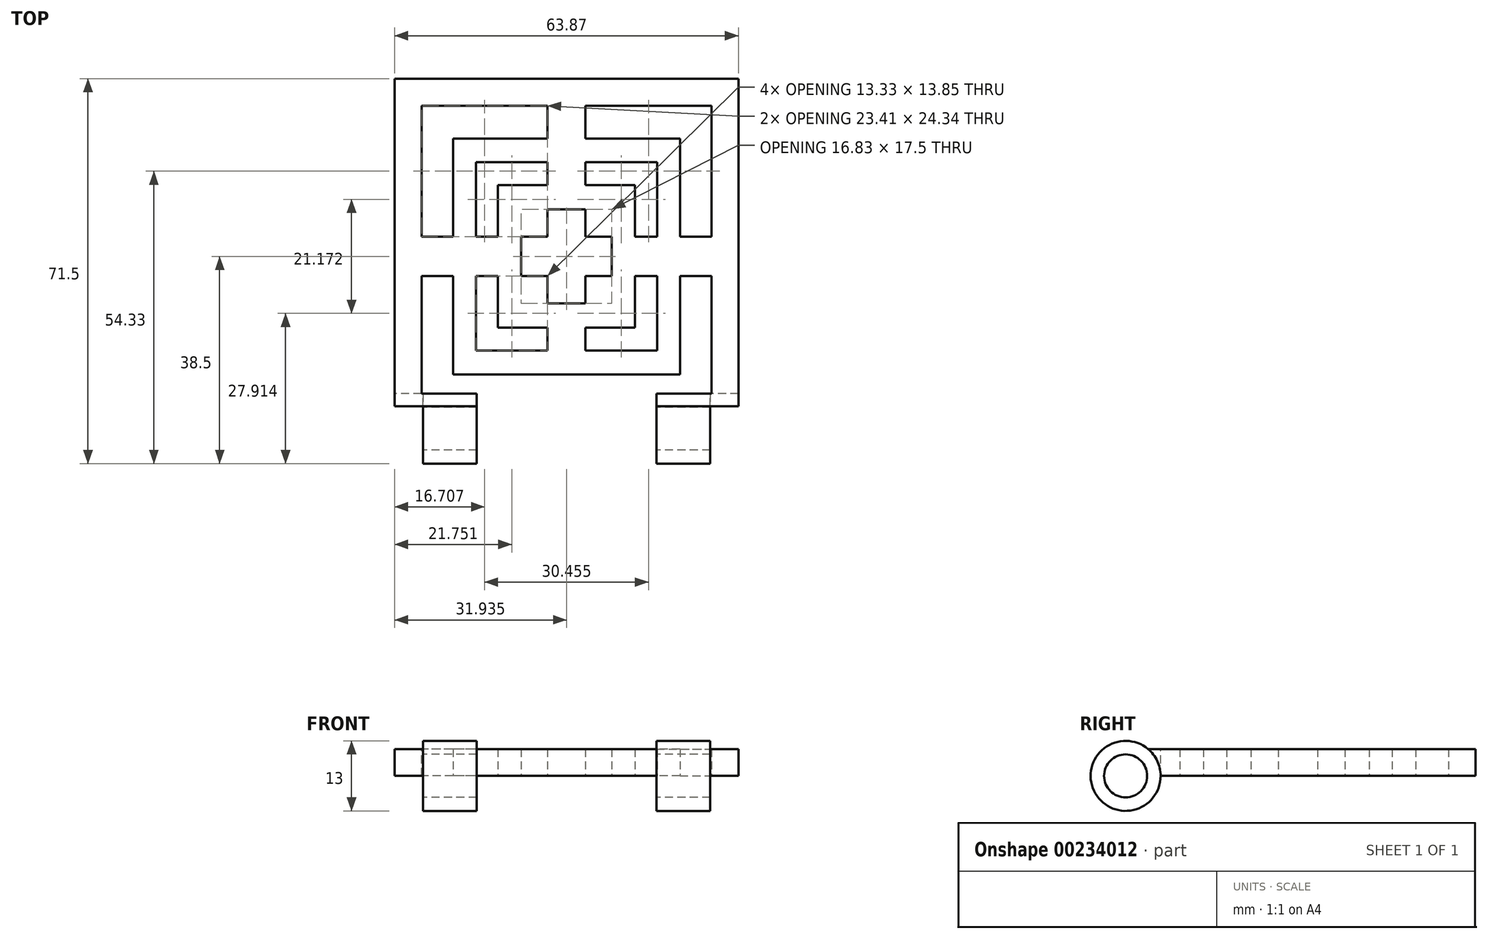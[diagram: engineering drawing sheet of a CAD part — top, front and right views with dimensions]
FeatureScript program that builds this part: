
annotation { "Feature Type Name" : "Feature", "Feature Type Description" : "" }
export const myFeature = defineFeature(function(context is Context, id is Id, definition is map)
    precondition{}
    {
        {
            var Q0;
            Q0=qCreatedBy(makeId("Top.planeOp"),FACE);
            var sketch = newSketch(context, id + "F0", { "sketchPlane" : qUnion([Q0])});
            skLineSegment(sketch, "E0.bottom", {"start": v(0, 0) * mm, "end": v(63.87, 0) * mm});
            skLineSegment(sketch, "E0.top", {"start": v(0, 61) * mm, "end": v(63.87, 61) * mm});
            skLineSegment(sketch, "E0.left", {"start": v(0, 0) * mm, "end": v(0, 61) * mm});
            skLineSegment(sketch, "E0.right", {"start": v(63.87, 0) * mm, "end": v(63.87, 61) * mm});
            skLineSegment(sketch, "E1.bottom", {"start": v(5, 0) * mm, "end": v(58.87, 0) * mm});
            skLineSegment(sketch, "E1.left", {"start": v(5, 0) * mm, "end": v(5, 56) * mm});
            skLineSegment(sketch, "E1.right", {"start": v(58.87, 0) * mm, "end": v(58.87, 56) * mm});
            skLineSegment(sketch, "E2", {"start": v(5, 56) * mm, "end": v(58.87, 56) * mm});
            skLineSegment(sketch, "E3", {"start": v(5, 56) * mm, "end": v(58.87, 0) * mm, "construction": true});
            skLineSegment(sketch, "E4", {"start": v(58.87, 56) * mm, "end": v(5, 0) * mm, "construction": true});
            skLineSegment(sketch, "E5.bottom", {"start": v(53, 49.9) * mm, "end": v(10.86, 49.9) * mm});
            skLineSegment(sketch, "E5.top", {"start": v(53, 6.1) * mm, "end": v(10.86, 6.1) * mm});
            skLineSegment(sketch, "E5.left", {"start": v(53, 49.9) * mm, "end": v(53, 6.1) * mm});
            skLineSegment(sketch, "E5.right", {"start": v(10.86, 49.9) * mm, "end": v(10.86, 6.1) * mm});
            skPoint(sketch, "E5.middle", {"position": v(31.93, 28) * mm});
            skLineSegment(sketch, "E6.bottom", {"start": v(48.78, 45.51) * mm, "end": v(15.09, 45.51) * mm});
            skLineSegment(sketch, "E6.top", {"start": v(48.78, 10.49) * mm, "end": v(15.09, 10.49) * mm});
            skLineSegment(sketch, "E6.left", {"start": v(48.78, 45.51) * mm, "end": v(48.78, 10.49) * mm});
            skLineSegment(sketch, "E6.right", {"start": v(15.09, 45.51) * mm, "end": v(15.09, 10.49) * mm});
            skLineSegment(sketch, "E7.bottom", {"start": v(44.66, 41.23) * mm, "end": v(19.21, 41.23) * mm});
            skLineSegment(sketch, "E7.top", {"start": v(44.66, 14.77) * mm, "end": v(19.21, 14.77) * mm});
            skLineSegment(sketch, "E7.left", {"start": v(44.66, 41.23) * mm, "end": v(44.66, 14.77) * mm});
            skLineSegment(sketch, "E7.right", {"start": v(19.21, 41.23) * mm, "end": v(19.21, 14.77) * mm});
            skLineSegment(sketch, "E8.bottom", {"start": v(40.35, 36.75) * mm, "end": v(23.52, 36.75) * mm});
            skLineSegment(sketch, "E8.top", {"start": v(40.35, 19.25) * mm, "end": v(23.52, 19.25) * mm});
            skLineSegment(sketch, "E8.left", {"start": v(40.35, 36.75) * mm, "end": v(40.35, 19.25) * mm});
            skLineSegment(sketch, "E8.right", {"start": v(23.52, 36.75) * mm, "end": v(23.52, 19.25) * mm});
            skLineSegment(sketch, "E9.bottom", {"start": v(35.46, 31.66) * mm, "end": v(28.41, 31.66) * mm, "construction": true});
            skLineSegment(sketch, "E9.top", {"start": v(35.46, 24.34) * mm, "end": v(28.41, 24.34) * mm, "construction": true});
            skLineSegment(sketch, "E9.left", {"start": v(35.46, 31.66) * mm, "end": v(35.46, 24.34) * mm, "construction": true});
            skLineSegment(sketch, "E9.right", {"start": v(28.41, 31.66) * mm, "end": v(28.41, 24.34) * mm, "construction": true});
            skLineSegment(sketch, "E10.bottom", {"start": v(28.41, 31.66) * mm, "end": v(5, 31.66) * mm});
            skLineSegment(sketch, "E10.top", {"start": v(28.41, 24.34) * mm, "end": v(5, 24.34) * mm});
            skLineSegment(sketch, "E10.right", {"start": v(5, 31.66) * mm, "end": v(5, 24.34) * mm, "construction": true});
            skLineSegment(sketch, "E11.bottom", {"start": v(28.41, 24.34) * mm, "end": v(35.46, 24.34) * mm, "construction": true});
            skLineSegment(sketch, "E11.top", {"start": v(28.41, 0) * mm, "end": v(35.46, 0) * mm, "construction": true});
            skLineSegment(sketch, "E11.left", {"start": v(28.41, 24.34) * mm, "end": v(28.41, 0) * mm});
            skLineSegment(sketch, "E11.right", {"start": v(35.46, 24.34) * mm, "end": v(35.46, 0) * mm});
            skLineSegment(sketch, "E12.bottom", {"start": v(35.46, 31.66) * mm, "end": v(58.87, 31.66) * mm});
            skLineSegment(sketch, "E12.top", {"start": v(35.46, 24.34) * mm, "end": v(58.87, 24.34) * mm});
            skLineSegment(sketch, "E12.right", {"start": v(58.87, 31.66) * mm, "end": v(58.87, 24.34) * mm, "construction": true});
            skLineSegment(sketch, "E13.top", {"start": v(35.46, 56) * mm, "end": v(28.41, 56) * mm, "construction": true});
            skLineSegment(sketch, "E13.left", {"start": v(35.46, 31.66) * mm, "end": v(35.46, 56) * mm});
            skLineSegment(sketch, "E13.right", {"start": v(28.41, 31.66) * mm, "end": v(28.41, 56) * mm});
            skSolve(sketch);
        }
        {
            var Q0;
            Q0=makeQuery(id+"F0.imprint","IMPRINT",FACE,{"disambiguationData":[TD([[makeQuery(id+"F0.imprint","IMPRINT",EDGE,{"derivedFrom":sQuery(id+"F0.wireOp",EDGE,"E0.top")}),-1.0]])]});
            var Q1;
            {var subQ7=sQuery(id+"F0.wireOp",EDGE,"E5.right");var subQ8=sQuery(id+"F0.wireOp",EDGE,"E5.bottom");var subQ9=makeQuery(id+"F0.imprint","INTERSECT",VERTEX,{"derivedFrom":[subQ8,subQ7]});Q1=makeQuery(id+"F0.imprint","IMPRINT",FACE,{"disambiguationData":[TD([[makeQuery(id+"F0.imprint","IMPRINT",EDGE,{"disambiguationData":[TD([[subQ9,1.0]])],"derivedFrom":subQ8}),1.0]])]});}
            var Q2;
            {var subQ0=sQuery(id+"F0.wireOp",EDGE,"E13.left");var subQ1=sQuery(id+"F0.wireOp",EDGE,"E2");var subQ2=makeQuery(id+"F0.imprint","INTERSECT",VERTEX,{"derivedFrom":[subQ1,subQ0]});Q2=makeQuery(id+"F0.imprint","IMPRINT",FACE,{"disambiguationData":[TD([[makeQuery(id+"F0.imprint","IMPRINT",EDGE,{"disambiguationData":[TD([[subQ2,1.0]])],"derivedFrom":subQ1}),-1.0]])]});}
            var Q3;
            {var subQ5=sQuery(id+"F0.wireOp",EDGE,"E5.left");var subQ9=sQuery(id+"F0.wireOp",EDGE,"E5.bottom");var subQ10=makeQuery(id+"F0.imprint","INTERSECT",VERTEX,{"derivedFrom":[subQ9,subQ5]});Q3=makeQuery(id+"F0.imprint","IMPRINT",FACE,{"disambiguationData":[TD([[makeQuery(id+"F0.imprint","IMPRINT",EDGE,{"disambiguationData":[TD([[subQ10,-1.0]])],"derivedFrom":subQ9}),1.0]])]});}
            var Q4;
            {var subQ0=sQuery(id+"F0.wireOp",EDGE,"E13.left");var subQ1=sQuery(id+"F0.wireOp",EDGE,"E5.bottom");var subQ2=makeQuery(id+"F0.imprint","INTERSECT",VERTEX,{"derivedFrom":[subQ1,subQ0]});Q4=makeQuery(id+"F0.imprint","IMPRINT",FACE,{"disambiguationData":[TD([[makeQuery(id+"F0.imprint","IMPRINT",EDGE,{"disambiguationData":[TD([[subQ2,-1.0]])],"derivedFrom":subQ1}),1.0]])]});}
            var Q5;
            {var subQ0=sQuery(id+"F0.wireOp",EDGE,"E10.bottom");var subQ1=sQuery(id+"F0.wireOp",EDGE,"E5.right");var subQ2=makeQuery(id+"F0.imprint","INTERSECT",VERTEX,{"derivedFrom":[subQ1,subQ0]});Q5=makeQuery(id+"F0.imprint","IMPRINT",FACE,{"disambiguationData":[TD([[makeQuery(id+"F0.imprint","IMPRINT",EDGE,{"disambiguationData":[TD([[subQ2,-1.0]])],"derivedFrom":subQ1}),1.0]])]});}
            var Q6;
            {var subQ7=sQuery(id+"F0.wireOp",EDGE,"E5.right");var subQ8=sQuery(id+"F0.wireOp",EDGE,"E5.top");var subQ9=makeQuery(id+"F0.imprint","INTERSECT",VERTEX,{"derivedFrom":[subQ8,subQ7]});Q6=makeQuery(id+"F0.imprint","IMPRINT",FACE,{"disambiguationData":[TD([[makeQuery(id+"F0.imprint","IMPRINT",EDGE,{"disambiguationData":[TD([[subQ9,1.0]])],"derivedFrom":subQ8}),-1.0]])]});}
            var Q7;
            {var subQ0=sQuery(id+"F0.wireOp",EDGE,"E11.right");var subQ1=sQuery(id+"F0.wireOp",EDGE,"E5.top");var subQ2=makeQuery(id+"F0.imprint","INTERSECT",VERTEX,{"derivedFrom":[subQ1,subQ0]});Q7=makeQuery(id+"F0.imprint","IMPRINT",FACE,{"disambiguationData":[TD([[makeQuery(id+"F0.imprint","IMPRINT",EDGE,{"disambiguationData":[TD([[subQ2,-1.0]])],"derivedFrom":subQ1}),-1.0]])]});}
            var Q8;
            {var subQ6=sQuery(id+"F0.wireOp",EDGE,"E5.left");var subQ9=sQuery(id+"F0.wireOp",EDGE,"E5.top");var subQ10=makeQuery(id+"F0.imprint","INTERSECT",VERTEX,{"derivedFrom":[subQ9,subQ6]});Q8=makeQuery(id+"F0.imprint","IMPRINT",FACE,{"disambiguationData":[TD([[makeQuery(id+"F0.imprint","IMPRINT",EDGE,{"disambiguationData":[TD([[subQ10,-1.0]])],"derivedFrom":subQ9}),-1.0]])]});}
            var Q9;
            {var subQ0=sQuery(id+"F0.wireOp",EDGE,"E12.bottom");var subQ1=sQuery(id+"F0.wireOp",EDGE,"E5.left");var subQ2=makeQuery(id+"F0.imprint","INTERSECT",VERTEX,{"derivedFrom":[subQ1,subQ0]});Q9=makeQuery(id+"F0.imprint","IMPRINT",FACE,{"disambiguationData":[TD([[makeQuery(id+"F0.imprint","IMPRINT",EDGE,{"disambiguationData":[TD([[subQ2,-1.0]])],"derivedFrom":subQ1}),-1.0]])]});}
            var Q10;
            {var subQ5=sQuery(id+"F0.wireOp",EDGE,"E7.left");var subQ6=sQuery(id+"F0.wireOp",EDGE,"E7.bottom");var subQ7=makeQuery(id+"F0.imprint","INTERSECT",VERTEX,{"derivedFrom":[subQ6,subQ5]});Q10=makeQuery(id+"F0.imprint","IMPRINT",FACE,{"disambiguationData":[TD([[makeQuery(id+"F0.imprint","IMPRINT",EDGE,{"disambiguationData":[TD([[subQ7,-1.0]])],"derivedFrom":subQ6}),1.0]])]});}
            var Q11;
            {var subQ0=sQuery(id+"F0.wireOp",EDGE,"E12.bottom");var subQ1=sQuery(id+"F0.wireOp",EDGE,"E7.left");var subQ2=makeQuery(id+"F0.imprint","INTERSECT",VERTEX,{"derivedFrom":[subQ1,subQ0]});Q11=makeQuery(id+"F0.imprint","IMPRINT",FACE,{"disambiguationData":[TD([[makeQuery(id+"F0.imprint","IMPRINT",EDGE,{"disambiguationData":[TD([[subQ2,-1.0]])],"derivedFrom":subQ1}),-1.0]])]});}
            var Q12;
            {var subQ7=sQuery(id+"F0.wireOp",EDGE,"E7.left");var subQ8=sQuery(id+"F0.wireOp",EDGE,"E7.top");var subQ9=makeQuery(id+"F0.imprint","INTERSECT",VERTEX,{"derivedFrom":[subQ8,subQ7]});Q12=makeQuery(id+"F0.imprint","IMPRINT",FACE,{"disambiguationData":[TD([[makeQuery(id+"F0.imprint","IMPRINT",EDGE,{"disambiguationData":[TD([[subQ9,-1.0]])],"derivedFrom":subQ8}),-1.0]])]});}
            var Q13;
            {var subQ7=sQuery(id+"F0.wireOp",EDGE,"E7.right");var subQ9=sQuery(id+"F0.wireOp",EDGE,"E7.top");var subQ10=makeQuery(id+"F0.imprint","INTERSECT",VERTEX,{"derivedFrom":[subQ9,subQ7]});Q13=makeQuery(id+"F0.imprint","IMPRINT",FACE,{"disambiguationData":[TD([[makeQuery(id+"F0.imprint","IMPRINT",EDGE,{"disambiguationData":[TD([[subQ10,1.0]])],"derivedFrom":subQ9}),-1.0]])]});}
            var Q14;
            {var subQ0=sQuery(id+"F0.wireOp",EDGE,"E11.right");var subQ1=sQuery(id+"F0.wireOp",EDGE,"E7.top");var subQ2=makeQuery(id+"F0.imprint","INTERSECT",VERTEX,{"derivedFrom":[subQ1,subQ0]});Q14=makeQuery(id+"F0.imprint","IMPRINT",FACE,{"disambiguationData":[TD([[makeQuery(id+"F0.imprint","IMPRINT",EDGE,{"disambiguationData":[TD([[subQ2,-1.0]])],"derivedFrom":subQ1}),-1.0]])]});}
            var Q15;
            {var subQ0=sQuery(id+"F0.wireOp",EDGE,"E11.right");var subQ1=sQuery(id+"F0.wireOp",EDGE,"E6.top");var subQ2=makeQuery(id+"F0.imprint","INTERSECT",VERTEX,{"derivedFrom":[subQ1,subQ0]});Q15=makeQuery(id+"F0.imprint","IMPRINT",FACE,{"disambiguationData":[TD([[makeQuery(id+"F0.imprint","IMPRINT",EDGE,{"disambiguationData":[TD([[subQ2,-1.0]])],"derivedFrom":subQ1}),-1.0]])]});}
            var Q16;
            {var subQ0=sQuery(id+"F0.wireOp",EDGE,"E10.bottom");var subQ1=sQuery(id+"F0.wireOp",EDGE,"E7.right");var subQ2=makeQuery(id+"F0.imprint","INTERSECT",VERTEX,{"derivedFrom":[subQ1,subQ0]});Q16=makeQuery(id+"F0.imprint","IMPRINT",FACE,{"disambiguationData":[TD([[makeQuery(id+"F0.imprint","IMPRINT",EDGE,{"disambiguationData":[TD([[subQ2,-1.0]])],"derivedFrom":subQ1}),1.0]])]});}
            var Q17;
            {var subQ7=sQuery(id+"F0.wireOp",EDGE,"E7.right");var subQ8=sQuery(id+"F0.wireOp",EDGE,"E7.bottom");var subQ9=makeQuery(id+"F0.imprint","INTERSECT",VERTEX,{"derivedFrom":[subQ8,subQ7]});Q17=makeQuery(id+"F0.imprint","IMPRINT",FACE,{"disambiguationData":[TD([[makeQuery(id+"F0.imprint","IMPRINT",EDGE,{"disambiguationData":[TD([[subQ9,1.0]])],"derivedFrom":subQ8}),1.0]])]});}
            var Q18;
            {var subQ0=sQuery(id+"F0.wireOp",EDGE,"E13.left");var subQ1=sQuery(id+"F0.wireOp",EDGE,"E7.bottom");var subQ2=makeQuery(id+"F0.imprint","INTERSECT",VERTEX,{"derivedFrom":[subQ1,subQ0]});Q18=makeQuery(id+"F0.imprint","IMPRINT",FACE,{"disambiguationData":[TD([[makeQuery(id+"F0.imprint","IMPRINT",EDGE,{"disambiguationData":[TD([[subQ2,-1.0]])],"derivedFrom":subQ1}),1.0]])]});}
            var Q19;
            {var subQ0=sQuery(id+"F0.wireOp",EDGE,"E12.bottom");var subQ1=sQuery(id+"F0.wireOp",EDGE,"E1.right");var subQ2=makeQuery(id+"F0.imprint","INTERSECT",VERTEX,{"derivedFrom":[subQ1,subQ0]});Q19=makeQuery(id+"F0.imprint","IMPRINT",FACE,{"disambiguationData":[TD([[makeQuery(id+"F0.imprint","IMPRINT",EDGE,{"disambiguationData":[TD([[subQ2,1.0]])],"derivedFrom":subQ1}),1.0]])]});}
            var Q20;
            {var subQ0=sQuery(id+"F0.wireOp",EDGE,"E12.bottom");var subQ1=sQuery(id+"F0.wireOp",EDGE,"E6.left");var subQ2=makeQuery(id+"F0.imprint","INTERSECT",VERTEX,{"derivedFrom":[subQ1,subQ0]});Q20=makeQuery(id+"F0.imprint","IMPRINT",FACE,{"disambiguationData":[TD([[makeQuery(id+"F0.imprint","IMPRINT",EDGE,{"disambiguationData":[TD([[subQ2,-1.0]])],"derivedFrom":subQ1}),-1.0]])]});}
            var Q21;
            {var subQ0=sQuery(id+"F0.wireOp",EDGE,"E10.bottom");var subQ1=sQuery(id+"F0.wireOp",EDGE,"E6.right");var subQ2=makeQuery(id+"F0.imprint","INTERSECT",VERTEX,{"derivedFrom":[subQ1,subQ0]});Q21=makeQuery(id+"F0.imprint","IMPRINT",FACE,{"disambiguationData":[TD([[makeQuery(id+"F0.imprint","IMPRINT",EDGE,{"disambiguationData":[TD([[subQ2,-1.0]])],"derivedFrom":subQ1}),1.0]])]});}
            var Q22;
            {var subQ0=sQuery(id+"F0.wireOp",EDGE,"E10.bottom");var subQ1=sQuery(id+"F0.wireOp",EDGE,"E1.left");var subQ2=makeQuery(id+"F0.imprint","INTERSECT",VERTEX,{"derivedFrom":[subQ1,subQ0]});Q22=makeQuery(id+"F0.imprint","IMPRINT",FACE,{"disambiguationData":[TD([[makeQuery(id+"F0.imprint","IMPRINT",EDGE,{"disambiguationData":[TD([[subQ2,1.0]])],"derivedFrom":subQ1}),-1.0]])]});}
            var Q23;
            {var subQ0=sQuery(id+"F0.wireOp",EDGE,"E13.left");var subQ1=sQuery(id+"F0.wireOp",EDGE,"E6.bottom");var subQ2=makeQuery(id+"F0.imprint","INTERSECT",VERTEX,{"derivedFrom":[subQ1,subQ0]});Q23=makeQuery(id+"F0.imprint","IMPRINT",FACE,{"disambiguationData":[TD([[makeQuery(id+"F0.imprint","IMPRINT",EDGE,{"disambiguationData":[TD([[subQ2,-1.0]])],"derivedFrom":subQ1}),1.0]])]});}
            var Q24;
            {var subQ0=sQuery(id+"F0.wireOp",EDGE,"E8.right");var subQ1=sQuery(id+"F0.wireOp",EDGE,"E8.bottom");var subQ2=makeQuery(id+"F0.imprint","INTERSECT",VERTEX,{"derivedFrom":[subQ1,subQ0]});Q24=makeQuery(id+"F0.imprint","IMPRINT",FACE,{"disambiguationData":[TD([[makeQuery(id+"F0.imprint","IMPRINT",EDGE,{"disambiguationData":[TD([[subQ2,1.0]])],"derivedFrom":subQ1}),1.0]])]});}
            var Q25;
            {var subQ0=sQuery(id+"F0.wireOp",EDGE,"E8.left");var subQ1=sQuery(id+"F0.wireOp",EDGE,"E8.bottom");var subQ2=makeQuery(id+"F0.imprint","INTERSECT",VERTEX,{"derivedFrom":[subQ1,subQ0]});Q25=makeQuery(id+"F0.imprint","IMPRINT",FACE,{"disambiguationData":[TD([[makeQuery(id+"F0.imprint","IMPRINT",EDGE,{"disambiguationData":[TD([[subQ2,-1.0]])],"derivedFrom":subQ1}),1.0]])]});}
            var Q26;
            {var subQ0=sQuery(id+"F0.wireOp",EDGE,"E8.left");var subQ1=sQuery(id+"F0.wireOp",EDGE,"E8.top");var subQ2=makeQuery(id+"F0.imprint","INTERSECT",VERTEX,{"derivedFrom":[subQ1,subQ0]});Q26=makeQuery(id+"F0.imprint","IMPRINT",FACE,{"disambiguationData":[TD([[makeQuery(id+"F0.imprint","IMPRINT",EDGE,{"disambiguationData":[TD([[subQ2,-1.0]])],"derivedFrom":subQ1}),-1.0]])]});}
            var Q27;
            {var subQ0=sQuery(id+"F0.wireOp",EDGE,"E8.right");var subQ1=sQuery(id+"F0.wireOp",EDGE,"E8.top");var subQ2=makeQuery(id+"F0.imprint","INTERSECT",VERTEX,{"derivedFrom":[subQ1,subQ0]});Q27=makeQuery(id+"F0.imprint","IMPRINT",FACE,{"disambiguationData":[TD([[makeQuery(id+"F0.imprint","IMPRINT",EDGE,{"disambiguationData":[TD([[subQ2,1.0]])],"derivedFrom":subQ1}),-1.0]])]});}
            extrude(context, id + "F1", {"entities" : qUnion([Q0, Q1, Q2, Q3, Q4, Q5, Q6, Q7, Q8, Q9, Q10, Q11, Q12, Q13, Q14, Q15, Q16, Q17, Q18, Q19, Q20, Q21, Q22, Q23, Q24, Q25, Q26, Q27]), "depth" : 5 * mm});
        }
        {
            var Q0;
            Q0=makeQuery(id+"F1.opExtrude","SWEPT_FACE",FACE,{"disambiguationData":[OSD([sQuery(id+"F0.wireOp",EDGE,"E0.left")])]});
            var sketch = newSketch(context, id + "F2", { "sketchPlane" : qUnion([Q0])});
            skCircle(sketch, "E14", {"center": v(4, 0) * mm, "radius": 4 * mm});
            skPoint(sketch, "E14.centerSnap0", {"position": v(0, 0) * mm});
            skCircle(sketch, "E15", {"center": v(4, 0) * mm, "radius": 6.5 * mm});
            skSolve(sketch);
        }
        {
            var Q0;
            Q0 = qSketchRegion(id + "F2", true);
            var Q1;
            Q1=makeQuery(id+"F1.opExtrude","SWEPT_FACE",FACE,{"disambiguationData":[OSD([sQuery(id+"F0.wireOp",EDGE,"E0.right")])]});
            extrude(context, id + "F3", {"entities" : qUnion([Q0]), "operationType" : NewBodyOperationType.ADD, "endBound" : BoundingType.UP_TO_SURFACE, "oppositeDirection" : true, "endBoundEntityFace" : qUnion([Q1]), "depth" : 25 * mm});
        }
        {
            var Q0;
            Q0=makeQuery(id+"F3.boolean.opBoolean","MERGE",FACE,{"derivedFrom":[makeQuery(id+"F1.opExtrude","SWEPT_FACE",FACE,{"disambiguationData":[OSD([sQuery(id+"F0.wireOp",EDGE,"E0.right")])]}),makeQuery(id+"F3.opExtrude","CAP_FACE",FACE,{"disambiguationData":[OSD([sQuery(id+"F2.wireOp",EDGE,"E14"),sQuery(id+"F2.wireOp",EDGE,"E15")])],"isStart":false})]});
            var sketch = newSketch(context, id + "F4", { "sketchPlane" : qUnion([Q0])});
            skCircle(sketch, "E16", {"center": v(-4, 0) * mm, "radius": 4 * mm});
            skCircle(sketch, "E17", {"center": v(-4, 0) * mm, "radius": 6.5 * mm});
            skSolve(sketch);
        }
        {
            var Q0;
            Q0 = qSketchRegion(id + "F4", true);
            extrude(context, id + "F5", {"entities" : qUnion([Q0]), "operationType" : NewBodyOperationType.REMOVE, "oppositeDirection" : true, "depth" : 5.25 * mm});
        }
        {
            var Q0;
            Q0=makeQuery(id+"F3.boolean.opBoolean","MERGE",FACE,{"derivedFrom":[makeQuery(id+"F1.opExtrude","SWEPT_FACE",FACE,{"disambiguationData":[OSD([sQuery(id+"F0.wireOp",EDGE,"E0.left")])]}),makeQuery(id+"F3.opExtrude","CAP_FACE",FACE,{"disambiguationData":[OSD([sQuery(id+"F2.wireOp",EDGE,"E14"),sQuery(id+"F2.wireOp",EDGE,"E15")])],"isStart":true})]});
            var sketch = newSketch(context, id + "F6", { "sketchPlane" : qUnion([Q0])});
            skCircle(sketch, "E18", {"center": v(4, 0) * mm, "radius": 4 * mm});
            skCircle(sketch, "E19", {"center": v(4, 0) * mm, "radius": 6.5 * mm});
            skSolve(sketch);
        }
        {
            var Q0;
            Q0 = qSketchRegion(id + "F6", true);
            extrude(context, id + "F7", {"entities" : qUnion([Q0]), "operationType" : NewBodyOperationType.REMOVE, "oppositeDirection" : true, "depth" : 5.25 * mm});
        }
        {
            var Q0;
            Q0=makeQuery(id+"F7.boolean.opBoolean","COPY",FACE,{"derivedFrom":makeQuery(id+"F7.opExtrude","CAP_FACE",FACE,{"disambiguationData":[OSD([sQuery(id+"F6.wireOp",EDGE,"E18"),sQuery(id+"F6.wireOp",EDGE,"E19")])],"isStart":false})});
            cPlane(context, id + "F8", {"entities" : qUnion([Q0]), "cplaneType" : CPlaneType.OFFSET, "offset" : 10 * mm, "oppositeDirection" : true, "width" : 150 * mm, "height" : 150 * mm});
        }
        {
            var Q0;
            Q0=qCreatedBy(id+"F8.planeOp",FACE);
            var sketch = newSketch(context, id + "F9", { "sketchPlane" : qUnion([Q0])});
            skCircle(sketch, "E20", {"center": v(4, 0) * mm, "radius": 4 * mm});
            skCircle(sketch, "E21", {"center": v(4, 0) * mm, "radius": 6.5 * mm});
            skSolve(sketch);
        }
        {
            var Q0;
            Q0 = qSketchRegion(id + "F9", true);
            extrude(context, id + "F10", {"entities" : qUnion([Q0]), "operationType" : NewBodyOperationType.REMOVE, "oppositeDirection" : true, "depth" : (33.5 - .13) * mm});
        }
        {
            var Q0;
            {var subQ0=sQuery(id+"F0.wireOp",EDGE,"E1.right");Q0=makeQuery(id+"F1.opExtrude","SWEPT_FACE",FACE,{"disambiguationData":[OSD([subQ0]),TDD([makeQuery(id+"F0.imprint","IMPRINT",EDGE,{"disambiguationData":[TD([[makeQuery(id+"F0.imprint","INTERSECT",VERTEX,{"derivedFrom":[subQ0,sQuery(id+"F0.wireOp",EDGE,"E12.top")]}),1.0]])],"derivedFrom":subQ0})])]});}
            var sketch = newSketch(context, id + "F11", { "sketchPlane" : qUnion([Q0])});
            skArc(sketch, "E22", {"start": v(-0.15, 5) * mm, "mid": v(-1.88, 2.76) * mm, "end": v(-2.5, 0) * mm});
            skLineSegment(sketch, "E23", {"start": v(-2.5, 0) * mm, "end": v(-2.5, 5) * mm});
            skLineSegment(sketch, "E24", {"start": v(-2.5, 5) * mm, "end": v(-0.15, 5) * mm});
            skSolve(sketch);
        }
        {
            var Q0;
            Q0 = qSketchRegion(id + "F11", true);
            extrude(context, id + "F12", {"entities" : qUnion([Q0]), "operationType" : NewBodyOperationType.ADD, "depth" : 10.25 * mm});
        }
        {
            var Q0;
            {var subQ0=sQuery(id+"F0.wireOp",EDGE,"E1.left");Q0=makeQuery(id+"F1.opExtrude","SWEPT_FACE",FACE,{"disambiguationData":[OSD([subQ0]),TDD([makeQuery(id+"F0.imprint","IMPRINT",EDGE,{"disambiguationData":[TD([[makeQuery(id+"F0.imprint","INTERSECT",VERTEX,{"derivedFrom":[subQ0,sQuery(id+"F0.wireOp",EDGE,"E10.top")]}),1.0]])],"derivedFrom":subQ0})])]});}
            var sketch = newSketch(context, id + "F13", { "sketchPlane" : qUnion([Q0])});
            skArc(sketch, "E25", {"start": v(2.5, 0) * mm, "mid": v(1.88, 2.76) * mm, "end": v(0.15, 5) * mm});
            skLineSegment(sketch, "E26", {"start": v(2.5, 0) * mm, "end": v(2.5, 5) * mm});
            skLineSegment(sketch, "E27", {"start": v(2.5, 5) * mm, "end": v(0.15, 5) * mm});
            skSolve(sketch);
        }
        {
            var Q0;
            Q0 = qSketchRegion(id + "F13", true);
            extrude(context, id + "F14", {"entities" : qUnion([Q0]), "operationType" : NewBodyOperationType.ADD, "depth" : 10.25 * mm});
        }
    });
